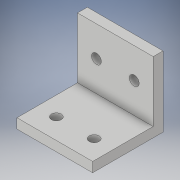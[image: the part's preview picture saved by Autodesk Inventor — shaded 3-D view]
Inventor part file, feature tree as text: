
AUTODESK INVENTOR PART (.ipt)
format: ipt  version: 2018 (Build 220112000, 112)  size: 120,320 bytes
history: native  units: in
note: dims shown in document units (in); Inventor stores cm internally (conversion verified against a paired STEP export)
features: sketch x4, extrude x2, hole x2
ambient origin geometry x8: Origin, YZ Plane, XZ Plane, XY Plane, X Axis, Y Axis, Z Axis, Center Point
bodies: Solid1 (feature_tree)
feature tree (8):
  extrude  "Extrusion1"  Depth=1.8307in
  extrude  "Extrusion2"  Depth=0.2559in
  hole  "Hole1"  [1 undecoded]
  hole  "Hole2"  [1 undecoded]
  sketch  "Sketch1"  dims[d0=1.9685in d1=1.8307in]
  sketch  "Sketch2"  dims[d2=0.2559in d3=0.2559in]
  sketch  "Sketch3"  dims[d4=0.2559in d5=0.0in d6=1.9685in]
  sketch  "Sketch4"  dims[d7=0.2559in d8=1.5748in d9=0.0in d10=0.2559in d11=0.2559in d12=0.2559in d13=0.2953in d14=0.1476in d15=0.0984in d16=90.0deg d17=0.3937in d18=0.8108in d19=0.2559in d20=0.2559in d21=0.2953in d22=0.1476in d23=0.0984in d24=90.0deg d25=0.3937in d26=0.8108in]
note: 2 required parameter values undecoded (feature->parameter linkage not recoverable at this tier; creation-order binding heuristic only, values carry confidence <= 0.55)
